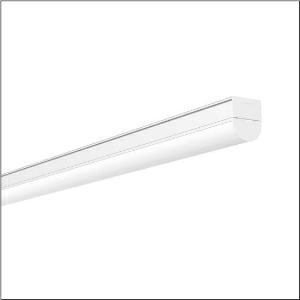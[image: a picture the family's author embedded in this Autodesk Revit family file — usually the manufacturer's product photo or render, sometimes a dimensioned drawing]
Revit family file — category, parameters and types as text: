
# Revit family: ecopack_r__31_51lj12dkm40a_26af
name_source: partatom
category: Lighting Fixtures
units: mm (PartAtom-declared; Revit-internal decimal feet)

## family parameters
Cut with Voids When Loaded = No
Host = Face
Light Source = No
Part Type = Normal
Room Calculation Point = No
Round Connector Dimension = Use Diameter
Shared = No

## types (1)
- --- (1 x LED, 4290 lm, 33 W, 5000K)
    Apparent Load = 33 VA
    CIE Flux Codes = 39 67 87 89 100
    Color Rendering = 80
    Color Temperature = 5000K
    Default Elevation = 1800 mm
    Description = Ecopack® 31, diffuser luminaire, primary optical cover: cover, of PC, frosted, light emission: direct distribution, primary light characteristic: symmetric, installation type: surface-mounted, LED, rated luminous flux: 4.300lm, luminous efficacy: 130lm/W, light colour: 830/840/850, colour temperature: 3000/4000/5000K, control gear: ECG DALI, with terminal, 5-pole, mains connection: 220..240V, AC, 50/60Hz, rated input power: 33W, housing, of aluminium, traffic white (RAL 9016), length: 1.150mm, width: 56mm, height: 68mm, end cap, of PC, white, protection rating (complete): IP20, insulation class (complete): insulation class I (protective earthing), certification: CE, impact resistance: IK06, permissible operating ambient temperature: -20..+40°C, packaging unit: 1 piece
    Height = 68 mm
    Lamp = 1 x LED
    Lamp Light Flux = 4290 lm
    Lamp Power = 33 W
    Lamp count = 1
    Length = 1149 mm
    Luminous efficacy = 130 lm/W
    Manufacturer = Siteco
    ModVariant = No
    Model = 51LJ12DKM40A
    Mounting Place = Ceiling
    Mounting Type = Surface mounted
    Number of Poles = 1
    OnlyDefault = Yes
    Power Factor = 1
    Product Name = Ecopack® 31
    Product group = diffuser luminaire
    ProductGroupID = 303
    Protection Class = Protection class I
    Protection Degree = IP 20
    RLX_Detail_Level = 1
    RLX_Emergency_Light_Flux = 0 lm
    RLX_Emergency_Type = 0
    RLX_Emergency_Type_DB = No
    RlxData = <blob elided: 24937 chars, md5=bd9987af>
    Socket = socket
    Standby Power = 0 W
    System Light Flux = 4290 lm
    System Power = 33 W
    Type Comments = individual setting: colour temperature 5000K
    Type Image = l_1007030.jpg
    URL = http://relux.com
    VarID = @adj_107075
    Voltage = 0 V
    Weight = 0.00 kg
    Width = 56 mm

## geometry (parser evidence)
native form markers: Blend x4, Sweep x12
no freeform markers — native parametric forms only
